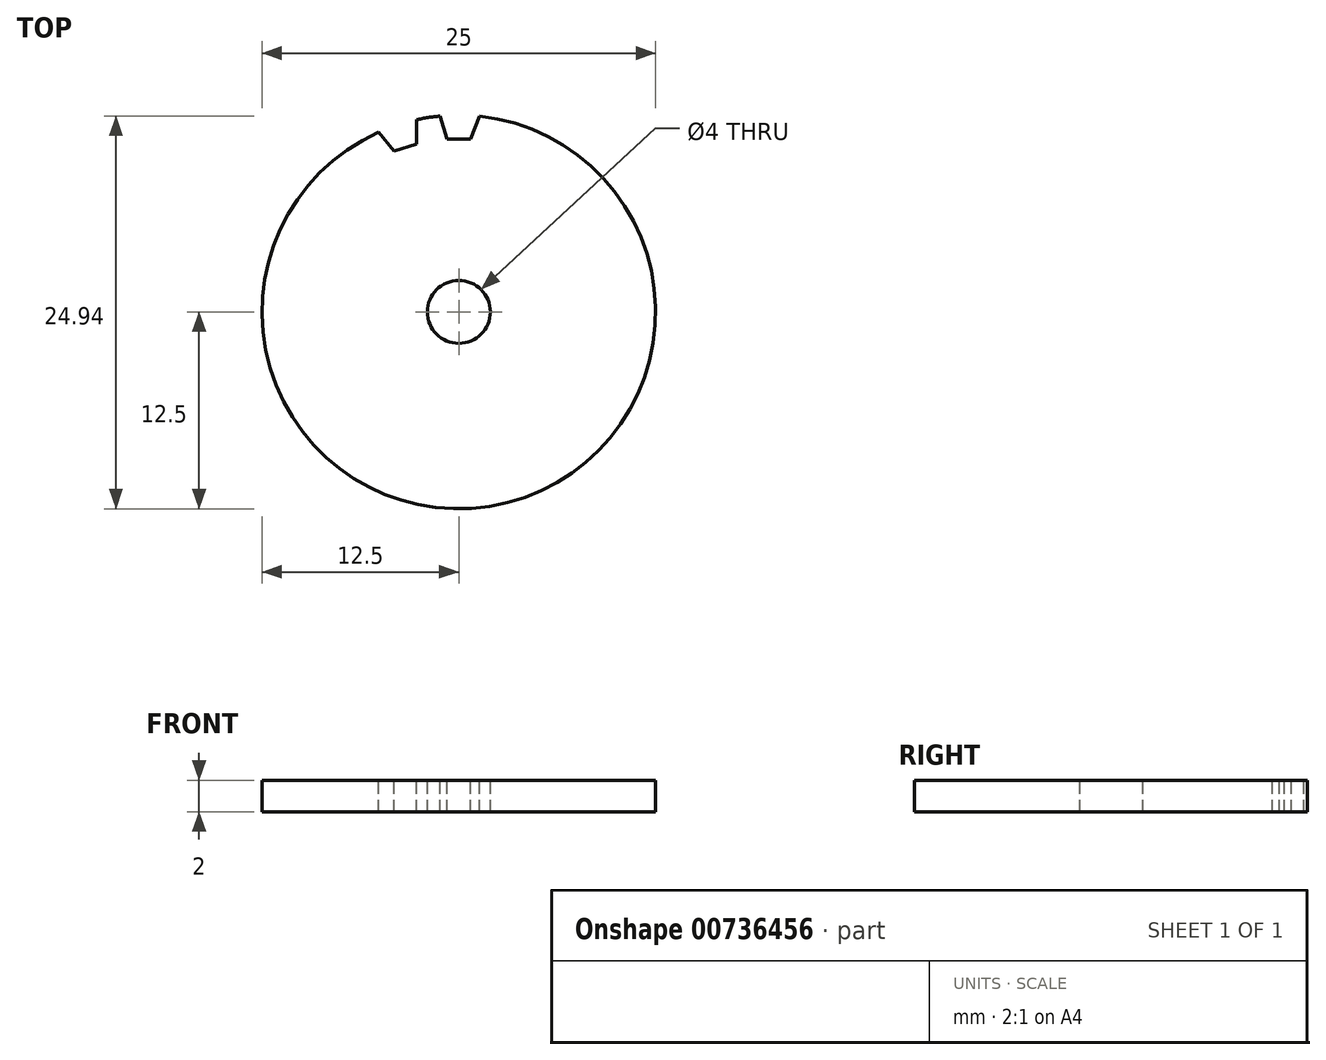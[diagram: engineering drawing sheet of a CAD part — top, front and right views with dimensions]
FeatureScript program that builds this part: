
annotation { "Feature Type Name" : "Feature", "Feature Type Description" : "" }
export const myFeature = defineFeature(function(context is Context, id is Id, definition is map)
    precondition{}
    {
        {
            var Q0;
            Q0=qCreatedBy(makeId("Top.planeOp"),FACE);
            var sketch = newSketch(context, id + "F0", { "sketchPlane" : qUnion([Q0])});
            skCircle(sketch, "E0", {"center": v(0, 0) * mm, "radius": 12.5 * mm});
            skSolve(sketch);
        }
        {
            var Q0;
            Q0=makeQuery(id+"F0.imprint","IMPRINT",FACE,{"disambiguationData":[TD([[makeQuery(id+"F0.imprint","IMPRINT",EDGE,{"derivedFrom":sQuery(id+"F0.wireOp",EDGE,"E0")}),1.0]])]});
            extrude(context, id + "F1", {"entities" : qUnion([Q0]), "oppositeDirection" : true, "depth" : 2 * mm, "offsetDistance" : 25 * mm});
        }
        {
            var Q0;
            Q0=qCreatedBy(makeId("Top.planeOp"),FACE);
            var sketch = newSketch(context, id + "F2", { "sketchPlane" : qUnion([Q0])});
            skLineSegment(sketch, "E1", {"start": v(0, 12.5) * mm, "end": v(0, 12.5) * mm});
            skLineSegment(sketch, "E2", {"start": v(0, 0) * mm, "end": v(0, 10.98) * mm, "construction": true});
            skCircle(sketch, "E3", {"center": v(0, 0) * mm, "radius": 12.5 * mm, "construction": true});
            skLineSegment(sketch, "E4", {"start": v(-2.68, 10.68) * mm, "end": v(-4.1, 10.21) * mm});
            skLineSegment(sketch, "E5", {"start": v(-0.75, 10.98) * mm, "end": v(0.75, 10.98) * mm});
            skLineSegment(sketch, "E6", {"start": v(0, 0) * mm, "end": v(-3.4, 10.44) * mm, "construction": true});
            skLineSegment(sketch, "E7", {"start": v(0.75, 10.98) * mm, "end": v(1.3, 12.43) * mm});
            skLineSegment(sketch, "E8", {"start": v(-4.1, 10.21) * mm, "end": v(-5.08, 11.42) * mm});
            skPoint(sketch, "E9.orphan", {"position": v(0, 12.5) * mm});
            skLineSegment(sketch, "E10", {"start": v(0, 0) * mm, "end": v(-1.4, 8.89) * mm});
            skLineSegment(sketch, "E11", {"start": v(-2.68, 10.68) * mm, "end": v(-2.7, 12.23) * mm});
            skLineSegment(sketch, "E12", {"start": v(-1.21, 12.46) * mm, "end": v(-0.75, 10.98) * mm});
            skLineSegment(sketch, "E13", {"start": v(-1.21, 12.46) * mm, "end": v(-2.7, 12.23) * mm});
            skLineSegment(sketch, "E14", {"start": v(-1.4, 8.89) * mm, "end": v(-1.96, 12.35) * mm});
            skLineSegment(sketch, "E15", {"start": v(1.3, 12.43) * mm, "end": v(-2.45, 15.1) * mm});
            skLineSegment(sketch, "E16", {"start": v(-2.45, 15.1) * mm, "end": v(-5.08, 11.42) * mm});
            skLineSegment(sketch, "E17", {"start": v(-2.45, 15.1) * mm, "end": v(-1.96, 12.35) * mm, "construction": true});
            skLineSegment(sketch, "E18", {"start": v(0, 12.5) * mm, "end": v(-3.86, 11.89) * mm});
            skSolve(sketch);
        }
        {
            var Q0;
            Q0=qCreatedBy(makeId("Front.planeOp"),FACE);
            var sketch = newSketch(context, id + "F3", { "sketchPlane" : qUnion([Q0])});
            skLineSegment(sketch, "E19", {"start": v(0, 0) * mm, "end": v(0, -5) * mm});
            skSolve(sketch);
        }
        {
            var Q0;
            Q0=qCreatedBy(makeId("Top.planeOp"),FACE);
            var sketch = newSketch(context, id + "F4", { "sketchPlane" : qUnion([Q0])});
            skCircle(sketch, "E20", {"center": v(0, 0) * mm, "radius": 2 * mm});
            skSolve(sketch);
        }
        {
            var Q0;
            Q0 = qSketchRegion(id + "F4", true);
            extrude(context, id + "F5", {"entities" : qUnion([Q0]), "operationType" : NewBodyOperationType.REMOVE, "endBound" : BoundingType.THROUGH_ALL, "oppositeDirection" : true, "depth" : 25 * mm, "offsetDistance" : 25 * mm});
        }
        {
            var Q0;
            Q0=makeQuery(id+"F2.imprint","IMPRINT",FACE,{"disambiguationData":[TD([[makeQuery(id+"F2.imprint","IMPRINT",EDGE,{"derivedFrom":sQuery(id+"F2.wireOp",EDGE,"E4")}),-1.0]])]});
            extrude(context, id + "F6", {"entities" : qUnion([Q0]), "operationType" : NewBodyOperationType.REMOVE, "oppositeDirection" : true, "depth" : 25 * mm, "offsetDistance" : 25 * mm});
        }
    });
